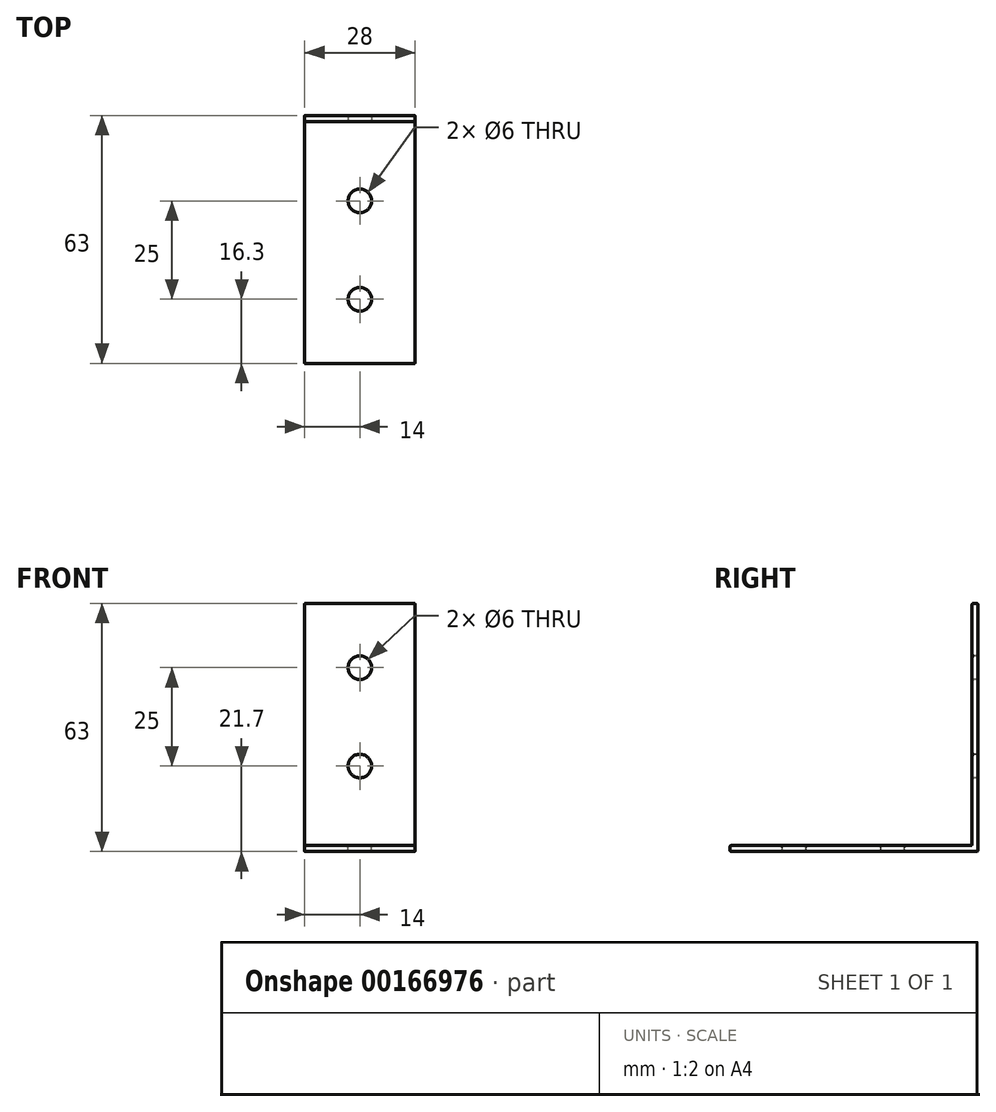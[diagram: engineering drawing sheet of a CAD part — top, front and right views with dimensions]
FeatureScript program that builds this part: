
annotation { "Feature Type Name" : "Feature", "Feature Type Description" : "" }
export const myFeature = defineFeature(function(context is Context, id is Id, definition is map)
    precondition{}
    {
        {
            var Q0;
            Q0=qCreatedBy(makeId("Top.planeOp"),FACE);
            var sketch = newSketch(context, id + "F0", { "sketchPlane" : qUnion([Q0])});
            skLineSegment(sketch, "E0.bottom", {"start": v(0, 0) * mm, "end": v(-28, 0) * mm});
            skLineSegment(sketch, "E0.top", {"start": v(0, -62.25) * mm, "end": v(-28, -62.25) * mm});
            skLineSegment(sketch, "E0.left", {"start": v(0, 0) * mm, "end": v(0, -62.25) * mm});
            skLineSegment(sketch, "E0.right", {"start": v(-28, 0) * mm, "end": v(-28, -62.25) * mm});
            skSolve(sketch);
        }
        {
            var Q0;
            Q0=qCreatedBy(makeId("Front.planeOp"),FACE);
            var sketch = newSketch(context, id + "F1", { "sketchPlane" : qUnion([Q0])});
            skLineSegment(sketch, "E1.bottom", {"start": v(0, 0) * mm, "end": v(-28, 0) * mm});
            skLineSegment(sketch, "E1.top", {"start": v(0, 62.25) * mm, "end": v(-28, 62.25) * mm});
            skLineSegment(sketch, "E1.left", {"start": v(0, 0) * mm, "end": v(0, 62.25) * mm});
            skLineSegment(sketch, "E1.right", {"start": v(-28, 0) * mm, "end": v(-28, 62.25) * mm});
            skSolve(sketch);
        }
        {
            var Q0;
            Q0=makeQuery(id+"F0.imprint","IMPRINT",FACE,{"disambiguationData":[TD([[makeQuery(id+"F0.imprint","IMPRINT",EDGE,{"derivedFrom":sQuery(id+"F0.wireOp",EDGE,"E0.bottom")}),1.0]])]});
            extrude(context, id + "F2", {"entities" : qUnion([Q0]), "endBound" : BoundingType.SYMMETRIC, "depth" : 1.5 * mm});
        }
        {
            var Q0;
            Q0=makeQuery(id+"F1.imprint","IMPRINT",FACE,{"disambiguationData":[TD([[makeQuery(id+"F1.imprint","IMPRINT",EDGE,{"derivedFrom":sQuery(id+"F1.wireOp",EDGE,"E1.bottom")}),-1.0]])]});
            extrude(context, id + "F3", {"entities" : qUnion([Q0]), "operationType" : NewBodyOperationType.ADD, "endBound" : BoundingType.SYMMETRIC, "depth" : 1.5 * mm});
        }
        {
            var Q0;
            Q0=makeQuery(id+"F3.opExtrude","SWEPT_FACE",FACE,{"disambiguationData":[OSD([sQuery(id+"F1.wireOp",EDGE,"E1.bottom")])]});
            var Q1;
            Q1=makeQuery(id+"F2.opExtrude","CAP_FACE",FACE,{"disambiguationData":[OSD([sQuery(id+"F0.wireOp",EDGE,"E0.bottom"),sQuery(id+"F0.wireOp",EDGE,"E0.top"),sQuery(id+"F0.wireOp",EDGE,"E0.left"),sQuery(id+"F0.wireOp",EDGE,"E0.right")])],"isStart":true});
            extrude(context, id + "F4", {"entities" : qUnion([Q0]), "operationType" : NewBodyOperationType.ADD, "endBound" : BoundingType.UP_TO_SURFACE, "endBoundEntityFace" : qUnion([Q1]), "depth" : 0.5 * mm});
        }
        {
            var Q0;
            Q0=makeQuery(id+"F4.opExtrude","CAP_EDGE",EDGE,{"disambiguationData":[OSD([sQuery(id+"F1.wireOp",EDGE,"E1.bottom")])],"isStart":false});
            var Q1;
            Q1=makeQuery(id+"F3.boolean.opBoolean","INTERSECT",EDGE,{"derivedFrom":[makeQuery(id+"F2.opExtrude","CAP_FACE",FACE,{"disambiguationData":[OSD([sQuery(id+"F0.wireOp",EDGE,"E0.bottom"),sQuery(id+"F0.wireOp",EDGE,"E0.top"),sQuery(id+"F0.wireOp",EDGE,"E0.left"),sQuery(id+"F0.wireOp",EDGE,"E0.right")])],"isStart":false}),makeQuery(id+"F3.opExtrude","CAP_FACE",FACE,{"disambiguationData":[OSD([sQuery(id+"F1.wireOp",EDGE,"E1.bottom"),sQuery(id+"F1.wireOp",EDGE,"E1.top"),sQuery(id+"F1.wireOp",EDGE,"E1.left"),sQuery(id+"F1.wireOp",EDGE,"E1.right")])],"isStart":false})]});
            var Q2;
            Q2=makeQuery(id+"F2.opExtrude","CAP_EDGE",EDGE,{"disambiguationData":[OSD([sQuery(id+"F0.wireOp",EDGE,"E0.top")])],"isStart":false});
            var Q3;
            Q3=makeQuery(id+"F2.opExtrude","CAP_EDGE",EDGE,{"disambiguationData":[OSD([sQuery(id+"F0.wireOp",EDGE,"E0.top")])],"isStart":true});
            var Q4;
            Q4=makeQuery(id+"F3.opExtrude","CAP_EDGE",EDGE,{"disambiguationData":[OSD([sQuery(id+"F1.wireOp",EDGE,"E1.top")])],"isStart":false});
            var Q5;
            Q5=makeQuery(id+"F3.opExtrude","CAP_EDGE",EDGE,{"disambiguationData":[OSD([sQuery(id+"F1.wireOp",EDGE,"E1.top")])],"isStart":true});
            fillet(context, id + "F5", {"entities" : qUnion([Q0, Q1, Q2, Q3, Q4, Q5]), "radius" : 0.3 * mm, "tangentPropagation" : true, "allowEdgeOverflow" : false});
        }
        {
            var Q0;
            Q0=makeQuery(id+"F2.opExtrude","CAP_FACE",FACE,{"disambiguationData":[OSD([sQuery(id+"F0.wireOp",EDGE,"E0.bottom"),sQuery(id+"F0.wireOp",EDGE,"E0.top"),sQuery(id+"F0.wireOp",EDGE,"E0.left"),sQuery(id+"F0.wireOp",EDGE,"E0.right")])],"isStart":false});
            var sketch = newSketch(context, id + "F6", { "sketchPlane" : qUnion([Q0])});
            skLineSegment(sketch, "E2", {"start": v(-14, -61.95) * mm, "end": v(-14, -1.05) * mm, "construction": true});
            skCircle(sketch, "E3", {"center": v(-14, -45.95) * mm, "radius": 3 * mm});
            skCircle(sketch, "E4", {"center": v(-14, -20.95) * mm, "radius": 3 * mm});
            skSolve(sketch);
        }
        {
            var Q0;
            Q0=makeQuery(id+"F6.imprint","IMPRINT",FACE,{"disambiguationData":[TD([[makeQuery(id+"F6.imprint","IMPRINT",EDGE,{"derivedFrom":sQuery(id+"F6.wireOp",EDGE,"E3")}),1.0]])]});
            var Q1;
            Q1=makeQuery(id+"F6.imprint","IMPRINT",FACE,{"disambiguationData":[TD([[makeQuery(id+"F6.imprint","IMPRINT",EDGE,{"derivedFrom":sQuery(id+"F6.wireOp",EDGE,"E4")}),1.0]])]});
            extrude(context, id + "F7", {"entities" : qUnion([Q0, Q1]), "operationType" : NewBodyOperationType.REMOVE, "oppositeDirection" : true, "depth" : 25 * mm});
        }
        {
            var Q0;
            Q0=makeQuery(id+"F3.opExtrude","CAP_FACE",FACE,{"disambiguationData":[OSD([sQuery(id+"F1.wireOp",EDGE,"E1.bottom"),sQuery(id+"F1.wireOp",EDGE,"E1.top"),sQuery(id+"F1.wireOp",EDGE,"E1.left"),sQuery(id+"F1.wireOp",EDGE,"E1.right")])],"isStart":false});
            var sketch = newSketch(context, id + "F8", { "sketchPlane" : qUnion([Q0])});
            skLineSegment(sketch, "E5", {"start": v(-14, 61.95) * mm, "end": v(-14, 1.05) * mm, "construction": true});
            skCircle(sketch, "E6", {"center": v(-14, 45.95) * mm, "radius": 3 * mm});
            skCircle(sketch, "E7", {"center": v(-14, 20.95) * mm, "radius": 3 * mm});
            skSolve(sketch);
        }
        {
            var Q0;
            Q0=makeQuery(id+"F8.imprint","IMPRINT",FACE,{"disambiguationData":[TD([[makeQuery(id+"F8.imprint","IMPRINT",EDGE,{"derivedFrom":sQuery(id+"F8.wireOp",EDGE,"E7")}),1.0]])]});
            var Q1;
            Q1=makeQuery(id+"F8.imprint","IMPRINT",FACE,{"disambiguationData":[TD([[makeQuery(id+"F8.imprint","IMPRINT",EDGE,{"derivedFrom":sQuery(id+"F8.wireOp",EDGE,"E6")}),1.0]])]});
            extrude(context, id + "F9", {"entities" : qUnion([Q0, Q1]), "operationType" : NewBodyOperationType.REMOVE, "oppositeDirection" : true, "depth" : 25 * mm});
        }
        {
            var Q0;
            Q0=makeQuery(id+"F7.boolean.opBoolean","COPY",FACE,{"derivedFrom":makeQuery(id+"F7.opExtrude","SWEPT_FACE",FACE,{"disambiguationData":[OSD([sQuery(id+"F6.wireOp",EDGE,"E3")])]})});
            var Q1;
            Q1=makeQuery(id+"F7.boolean.opBoolean","COPY",FACE,{"derivedFrom":makeQuery(id+"F7.opExtrude","SWEPT_FACE",FACE,{"disambiguationData":[OSD([sQuery(id+"F6.wireOp",EDGE,"E4")])]})});
            var Q2;
            Q2=makeQuery(id+"F9.boolean.opBoolean","COPY",FACE,{"derivedFrom":makeQuery(id+"F9.opExtrude","SWEPT_FACE",FACE,{"disambiguationData":[OSD([sQuery(id+"F8.wireOp",EDGE,"E7")])]})});
            var Q3;
            Q3=makeQuery(id+"F9.boolean.opBoolean","COPY",FACE,{"derivedFrom":makeQuery(id+"F9.opExtrude","SWEPT_FACE",FACE,{"disambiguationData":[OSD([sQuery(id+"F8.wireOp",EDGE,"E6")])]})});
            fillet(context, id + "F10", {"entities" : qUnion([Q0, Q1, Q2, Q3]), "radius" : 0.4 * mm, "tangentPropagation" : true, "allowEdgeOverflow" : false});
        }
    });
